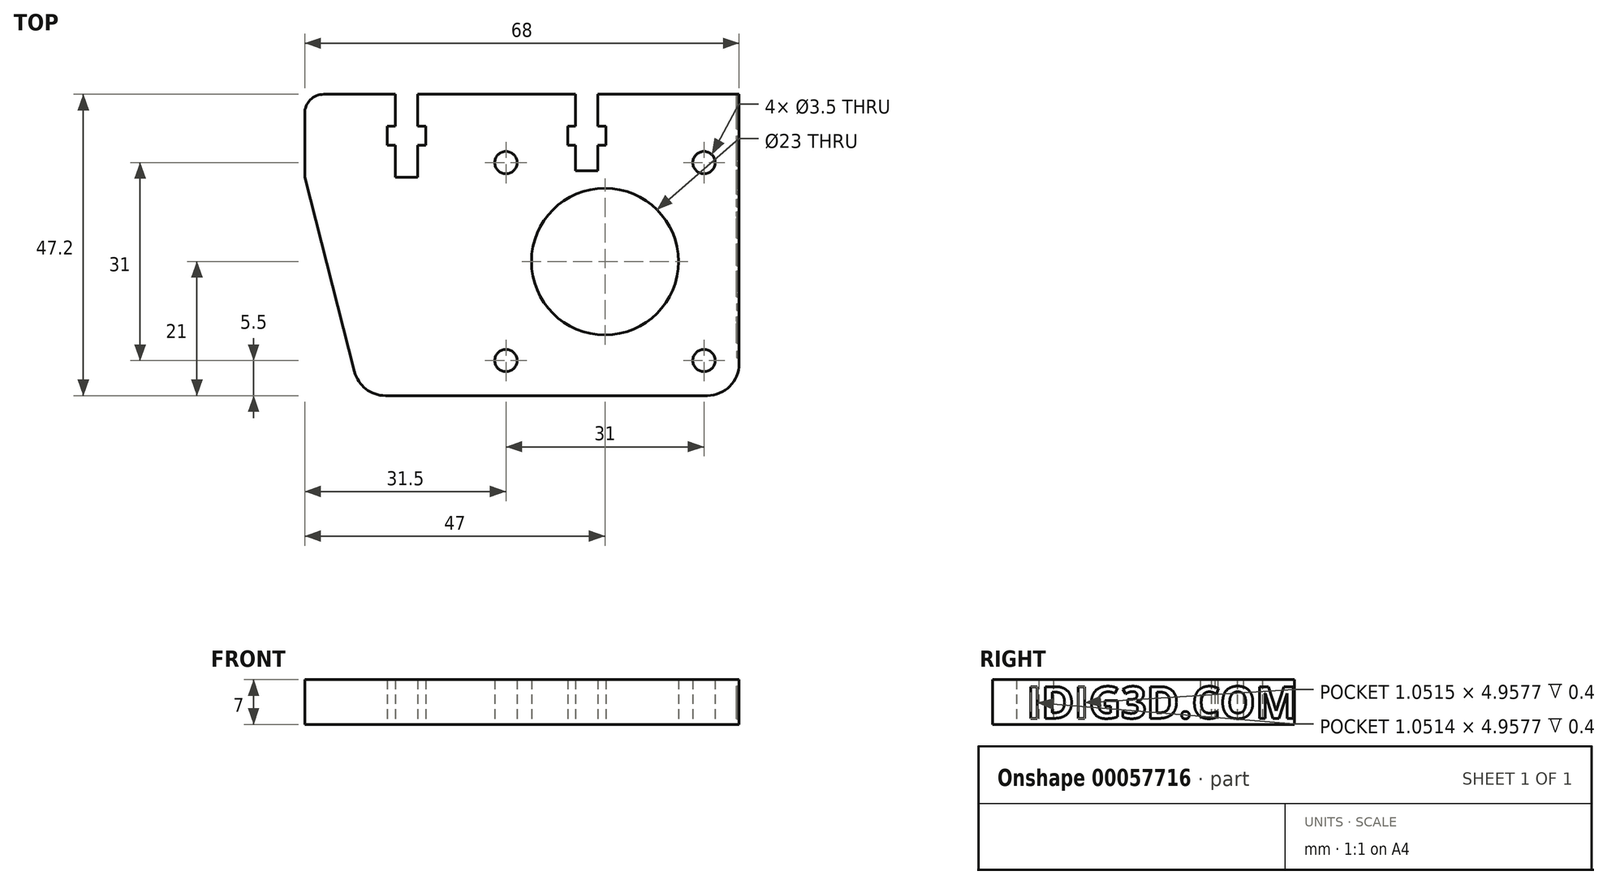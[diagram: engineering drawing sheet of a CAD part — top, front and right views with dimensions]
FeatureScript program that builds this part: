
annotation { "Feature Type Name" : "Feature", "Feature Type Description" : "" }
export const myFeature = defineFeature(function(context is Context, id is Id, definition is map)
    precondition{}
    {
        {
            var Q0;
            Q0=qCreatedBy(makeId("Top.planeOp"),FACE);
            var sketch = newSketch(context, id + "F0", { "sketchPlane" : qUnion([Q0])});
            skLineSegment(sketch, "E0.rect.bottom", {"start": v(-31, 23.6) * mm, "end": v(34, 23.6) * mm});
            skLineSegment(sketch, "E0.rect.top", {"start": v(-21.36, -23.6) * mm, "end": v(29, -23.6) * mm});
            skLineSegment(sketch, "E0.rect.left", {"start": v(-34, 20.6) * mm, "end": v(-34, 10.6) * mm});
            skLineSegment(sketch, "E0.rect.right", {"start": v(34, 23.6) * mm, "end": v(34, -18.6) * mm});
            skPoint(sketch, "E0.rect.middle", {"position": v(0, 0) * mm});
            skCircle(sketch, "E1", {"center": v(13, -2.6) * mm, "radius": 11.5 * mm});
            skLineSegment(sketch, "E2.rect.bottom", {"start": v(-2.5, 12.9) * mm, "end": v(28.5, 12.9) * mm, "construction": true});
            skLineSegment(sketch, "E2.rect.top", {"start": v(-2.5, -18.1) * mm, "end": v(28.5, -18.1) * mm, "construction": true});
            skLineSegment(sketch, "E2.rect.left", {"start": v(-2.5, 12.9) * mm, "end": v(-2.5, -18.1) * mm, "construction": true});
            skLineSegment(sketch, "E2.rect.right", {"start": v(28.5, 12.9) * mm, "end": v(28.5, -18.1) * mm, "construction": true});
            skCircle(sketch, "E3", {"center": v(-2.5, 12.9) * mm, "radius": 1.75 * mm});
            skCircle(sketch, "E4", {"center": v(28.5, 12.9) * mm, "radius": 1.75 * mm});
            skCircle(sketch, "E5", {"center": v(28.5, -18.1) * mm, "radius": 1.75 * mm});
            skCircle(sketch, "E6", {"center": v(-2.5, -18.1) * mm, "radius": 1.75 * mm});
            skPoint(sketch, "E7.visualSharp", {"position": v(-34, -23.6) * mm});
            skPoint(sketch, "E8.visualSharp", {"position": v(34, -23.6) * mm});
            skArc(sketch, "E8.filletArc", {"start": v(29, -23.6) * mm, "mid": v(32.54, -22.14) * mm, "end": v(34, -18.6) * mm});
            skLineSegment(sketch, "E9.rect.bottom", {"start": v(11.9, 23.6) * mm, "end": v(8.4, 23.6) * mm});
            skLineSegment(sketch, "E9.rect.top", {"start": v(11.9, 10.6) * mm, "end": v(8.4, 10.6) * mm});
            skLineSegment(sketch, "E9.rect.left", {"start": v(11.9, 23.6) * mm, "end": v(11.9, 10.6) * mm});
            skLineSegment(sketch, "E9.rect.right", {"start": v(8.4, 23.6) * mm, "end": v(8.4, 10.6) * mm});
            skPoint(sketch, "E9.rect.middle", {"position": v(10.15, 17.1) * mm});
            skLineSegment(sketch, "E10.rect.bottom", {"start": v(13.15, 18.6) * mm, "end": v(7.15, 18.6) * mm});
            skLineSegment(sketch, "E10.rect.top", {"start": v(13.15, 15.6) * mm, "end": v(7.15, 15.6) * mm});
            skLineSegment(sketch, "E10.rect.left", {"start": v(13.15, 18.6) * mm, "end": v(13.15, 15.6) * mm});
            skLineSegment(sketch, "E10.rect.right", {"start": v(7.15, 18.6) * mm, "end": v(7.15, 15.6) * mm});
            skPoint(sketch, "E10.rect.middle.positionSnap0", {"position": v(10.15, 10.6) * mm});
            skPoint(sketch, "E10.rect.centerSnap0", {"position": v(10.15, 10.6) * mm});
            skLineSegment(sketch, "E11.bottom", {"start": v(34, 23.6) * mm, "end": v(18.9, 23.6) * mm});
            skLineSegment(sketch, "E11.top", {"start": v(27, 30.6) * mm, "end": v(18.9, 30.6) * mm});
            skLineSegment(sketch, "E11.left", {"start": v(34, 23.6) * mm, "end": v(34, 23.6) * mm});
            skLineSegment(sketch, "E11.right", {"start": v(18.9, 23.6) * mm, "end": v(18.9, 30.6) * mm});
            skLineSegment(sketch, "E12.bottom", {"start": v(3.6, 23.6) * mm, "end": v(-11.6, 23.6) * mm});
            skLineSegment(sketch, "E12.top", {"start": v(3.6, 30.6) * mm, "end": v(-11.6, 30.6) * mm});
            skLineSegment(sketch, "E12.left", {"start": v(3.6, 23.6) * mm, "end": v(3.6, 30.6) * mm});
            skLineSegment(sketch, "E12.right", {"start": v(-11.6, 23.6) * mm, "end": v(-11.6, 30.6) * mm});
            skLineSegment(sketch, "E13.rect.left", {"start": v(-16.3, 23.6) * mm, "end": v(-16.3, 10.6) * mm});
            skLineSegment(sketch, "E13.rect.bottom", {"start": v(-16.3, 23.6) * mm, "end": v(-19.8, 23.6) * mm});
            skLineSegment(sketch, "E14.rect.right", {"start": v(-21.05, 18.6) * mm, "end": v(-21.05, 15.6) * mm});
            skLineSegment(sketch, "E14.rect.left", {"start": v(-15.05, 18.6) * mm, "end": v(-15.05, 15.6) * mm});
            skLineSegment(sketch, "E14.rect.bottom", {"start": v(-15.05, 18.6) * mm, "end": v(-21.05, 18.6) * mm});
            skLineSegment(sketch, "E13.rect.right", {"start": v(-19.8, 23.6) * mm, "end": v(-19.8, 10.6) * mm});
            skPoint(sketch, "E14.rect.centerSnap0", {"position": v(-18.05, 10.6) * mm});
            skLineSegment(sketch, "E14.rect.top", {"start": v(-15.05, 15.6) * mm, "end": v(-21.05, 15.6) * mm});
            skPoint(sketch, "E14.rect.middle.positionSnap0", {"position": v(-18.05, 10.6) * mm});
            skLineSegment(sketch, "E13.rect.top", {"start": v(-16.3, 10.6) * mm, "end": v(-19.8, 10.6) * mm});
            skPoint(sketch, "E15.visualSharp", {"position": v(34, 30.6) * mm});
            skArc(sketch, "E15.filletArc", {"start": v(34, 23.6) * mm, "mid": v(31.95, 28.55) * mm, "end": v(27, 30.6) * mm});
            skPoint(sketch, "E16.visualSharp", {"position": v(-34, 23.6) * mm});
            skArc(sketch, "E16.filletArc", {"start": v(-31, 23.6) * mm, "mid": v(-33.12, 22.72) * mm, "end": v(-34, 20.6) * mm});
            skLineSegment(sketch, "E17", {"start": v(-26.2, -19.84) * mm, "end": v(-34, 10.6) * mm});
            skPoint(sketch, "E18.visualSharp", {"position": v(-25.24, -23.6) * mm});
            skArc(sketch, "E18.filletArc", {"start": v(-26.2, -19.84) * mm, "mid": v(-24.43, -22.55) * mm, "end": v(-21.36, -23.6) * mm});
            skSolve(sketch);
        }
        {
            var Q0;
            Q0=makeQuery(id+"F0.imprint","IMPRINT",FACE,{"disambiguationData":[TD([[makeQuery(id+"F0.imprint","IMPRINT",EDGE,{"derivedFrom":sQuery(id+"F0.wireOp",EDGE,"7572a54b-43ae-45de-a91a-ef0717ead9ee.bottom")}),1.0]])]});
            var Q1;
            Q1=makeQuery(id+"F0.imprint","IMPRINT",FACE,{"disambiguationData":[TD([[makeQuery(id+"F0.imprint","IMPRINT",EDGE,{"derivedFrom":sQuery(id+"F0.wireOp",EDGE,"55d0d77d-85e9-44cf-bb75-9fa0512f92f50.MirrorCS")}),1.0]])]});
            var Q2;
            Q2=makeQuery(id+"F0.imprint","IMPRINT",FACE,{"disambiguationData":[TD([[makeQuery(id+"F0.imprint","IMPRINT",EDGE,{"derivedFrom":sQuery(id+"F0.wireOp",EDGE,"E0.rect.top")}),1.0]])]});
            var Q3;
            Q3=makeQuery(id+"F0.imprint","IMPRINT",FACE,{"disambiguationData":[TD([[makeQuery(id+"F0.imprint","IMPRINT",EDGE,{"derivedFrom":sQuery(id+"F0.wireOp",EDGE,"E12.bottom")}),-1.0]])]});
            var Q4;
            Q4=makeQuery(id+"F0.imprint","IMPRINT",FACE,{"disambiguationData":[TD([[makeQuery(id+"F0.imprint","IMPRINT",EDGE,{"derivedFrom":sQuery(id+"F0.wireOp",EDGE,"E11.bottom")}),-1.0]])]});
            extrude(context, id + "F1", {"entities" : qUnion([Q0, Q1, Q2, Q3, Q4]), "depth" : 7 * mm});
        }
        {
            var Q0;
            Q0=makeQuery(id+"F1.opExtrude","SWEPT_FACE",FACE,{"disambiguationData":[OSD([sQuery(id+"F0.wireOp",EDGE,"E0.rect.right")])]});
            var sketch = newSketch(context, id + "F2", { "sketchPlane" : qUnion([Q0])});
            skText(sketch, "E19", { "text": "IDIG3D.COM", "fontName": "OpenSans-Bold.ttf"});
            skPoint(sketch, "E20.0", {"position": v(0, 0) * mm});
            const initialGuessF2  = {"E19": [-0.01829, 0.00096, 1, 0, 0.005]};
            skSetInitialGuess(sketch, initialGuessF2);
            skSolve(sketch);
        }
        {
            var Q0;
            Q0=qSketchRegion(id+"F2",true);
            extrude(context, id + "F3", {"entities" : qUnion([Q0]), "operationType" : NewBodyOperationType.REMOVE, "oppositeDirection" : true, "depth" : .4 * mm});
        }
        {
            var Q0;
            Q0=makeQuery(id+"F1.opExtrude","SWEPT_FACE",FACE,{"disambiguationData":[OSD([sQuery(id+"F0.wireOp",EDGE,"E9.rect.top")])]});
            extrude(context, id + "F4", {"entities" : qUnion([Q0]), "operationType" : NewBodyOperationType.ADD, "depth" : 1 * mm});
        }
    });
